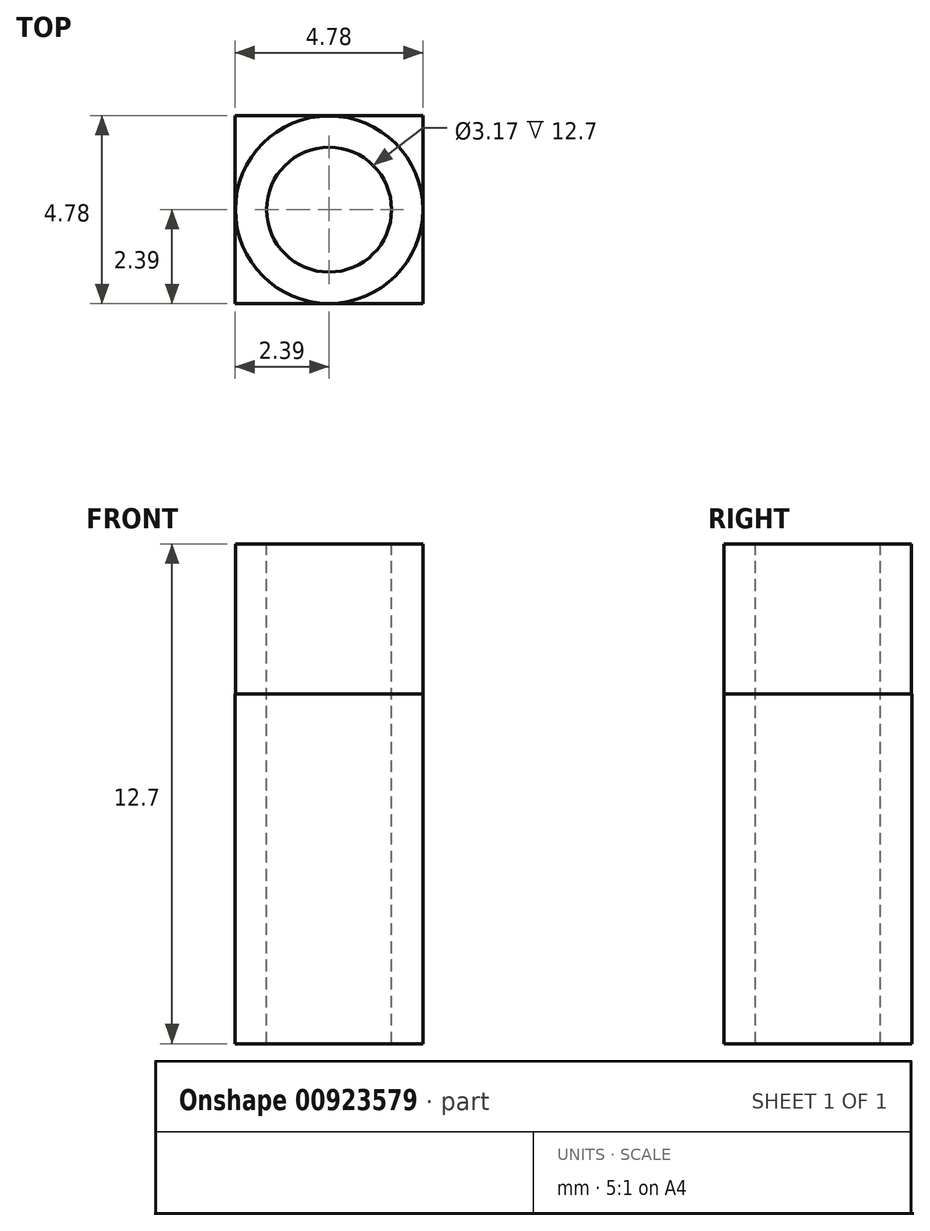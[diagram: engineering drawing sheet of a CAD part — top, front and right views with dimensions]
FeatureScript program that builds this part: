
annotation { "Feature Type Name" : "Feature", "Feature Type Description" : "" }
export const myFeature = defineFeature(function(context is Context, id is Id, definition is map)
    precondition{}
    {
        {
            var Q0;
            Q0=qCreatedBy(makeId("Top.planeOp"),FACE);
            var sketch = newSketch(context, id + "F0", { "sketchPlane" : qUnion([Q0])});
            skCircle(sketch, "E0", {"center": v(0, 0) * mm, "radius": 2.38 * mm});
            skSolve(sketch);
        }
        {
            var Q0;
            Q0=makeQuery(id+"F0.imprint","IMPRINT",FACE,{"disambiguationData":[TD([[makeQuery(id+"F0.imprint","IMPRINT",EDGE,{"derivedFrom":sQuery(id+"F0.wireOp",EDGE,"E0")}),1.0]])]});
            extrude(context, id + "F1", {"entities" : qUnion([Q0]), "depth" : 6.35 * mm, "offsetDistance" : 25.4 * mm});
        }
        {
            var Q0;
            Q0=makeQuery(id+"F1.opExtrude","CAP_FACE",FACE,{"disambiguationData":[OSD([sQuery(id+"F0.wireOp",EDGE,"E0")])],"isStart":false});
            var sketch = newSketch(context, id + "F2", { "sketchPlane" : qUnion([Q0])});
            skCircle(sketch, "E1", {"center": v(0, 0) * mm, "radius": 1.59 * mm});
            skSolve(sketch);
        }
        {
            var Q0;
            Q0=makeQuery(id+"F2.imprint","IMPRINT",FACE,{"disambiguationData":[TD([[makeQuery(id+"F2.imprint","IMPRINT",EDGE,{"derivedFrom":sQuery(id+"F2.wireOp",EDGE,"E1")}),1.0]])]});
            extrude(context, id + "F3", {"entities" : qUnion([Q0]), "operationType" : NewBodyOperationType.REMOVE, "oppositeDirection" : true, "depth" : 6.35 * mm, "offsetDistance" : 25.4 * mm});
        }
        {
            var Q0;
            Q0=makeQuery(id+"F1.opExtrude","CAP_FACE",FACE,{"disambiguationData":[OSD([sQuery(id+"F0.wireOp",EDGE,"E0")])],"isStart":true});
            var sketch = newSketch(context, id + "F4", { "sketchPlane" : qUnion([Q0])});
            skLineSegment(sketch, "E2.bottom", {"start": v(-2.39, -2.39) * mm, "end": v(2.39, -2.39) * mm});
            skLineSegment(sketch, "E2.top", {"start": v(-2.39, 2.39) * mm, "end": v(2.39, 2.39) * mm});
            skLineSegment(sketch, "E2.left", {"start": v(-2.39, -2.39) * mm, "end": v(-2.39, 2.39) * mm});
            skLineSegment(sketch, "E2.right", {"start": v(2.39, -2.39) * mm, "end": v(2.39, 2.39) * mm});
            skPoint(sketch, "E2.middle", {"position": v(0, 0) * mm});
            skSolve(sketch);
        }
        {
            var Q0;
            Q0=makeQuery(id+"F4.imprint","IMPRINT",FACE,{"disambiguationData":[TD([[makeQuery(id+"F4.imprint","IMPRINT",EDGE,{"derivedFrom":sQuery(id+"F4.wireOp",EDGE,"E2.bottom")}),1.0]])]});
            extrude(context, id + "F5", {"entities" : qUnion([Q0]), "operationType" : NewBodyOperationType.ADD, "oppositeDirection" : true, "depth" : 2.54 * mm, "offsetDistance" : 25.4 * mm});
        }
        {
            var Q0;
            {var subQ0=sQuery(id+"F0.wireOp",EDGE,"E0");Q0=makeQuery(id+"F5.boolean.opBoolean","MERGE",FACE,{"derivedFrom":[makeQuery(id+"F1.opExtrude","CAP_FACE",FACE,{"disambiguationData":[OSD([subQ0])],"isStart":true}),makeQuery(id+"F5.opExtrude","CAP_FACE",FACE,{"disambiguationData":[OSD([subQ0,sQuery(id+"F4.wireOp",EDGE,"E2.bottom"),sQuery(id+"F4.wireOp",EDGE,"E2.top"),sQuery(id+"F4.wireOp",EDGE,"E2.left"),sQuery(id+"F4.wireOp",EDGE,"E2.right")])],"isStart":true})]});}
            extrude(context, id + "F6", {"entities" : qUnion([Q0]), "operationType" : NewBodyOperationType.ADD, "depth" : 6.35 * mm, "offsetDistance" : 25.4 * mm});
        }
    });
